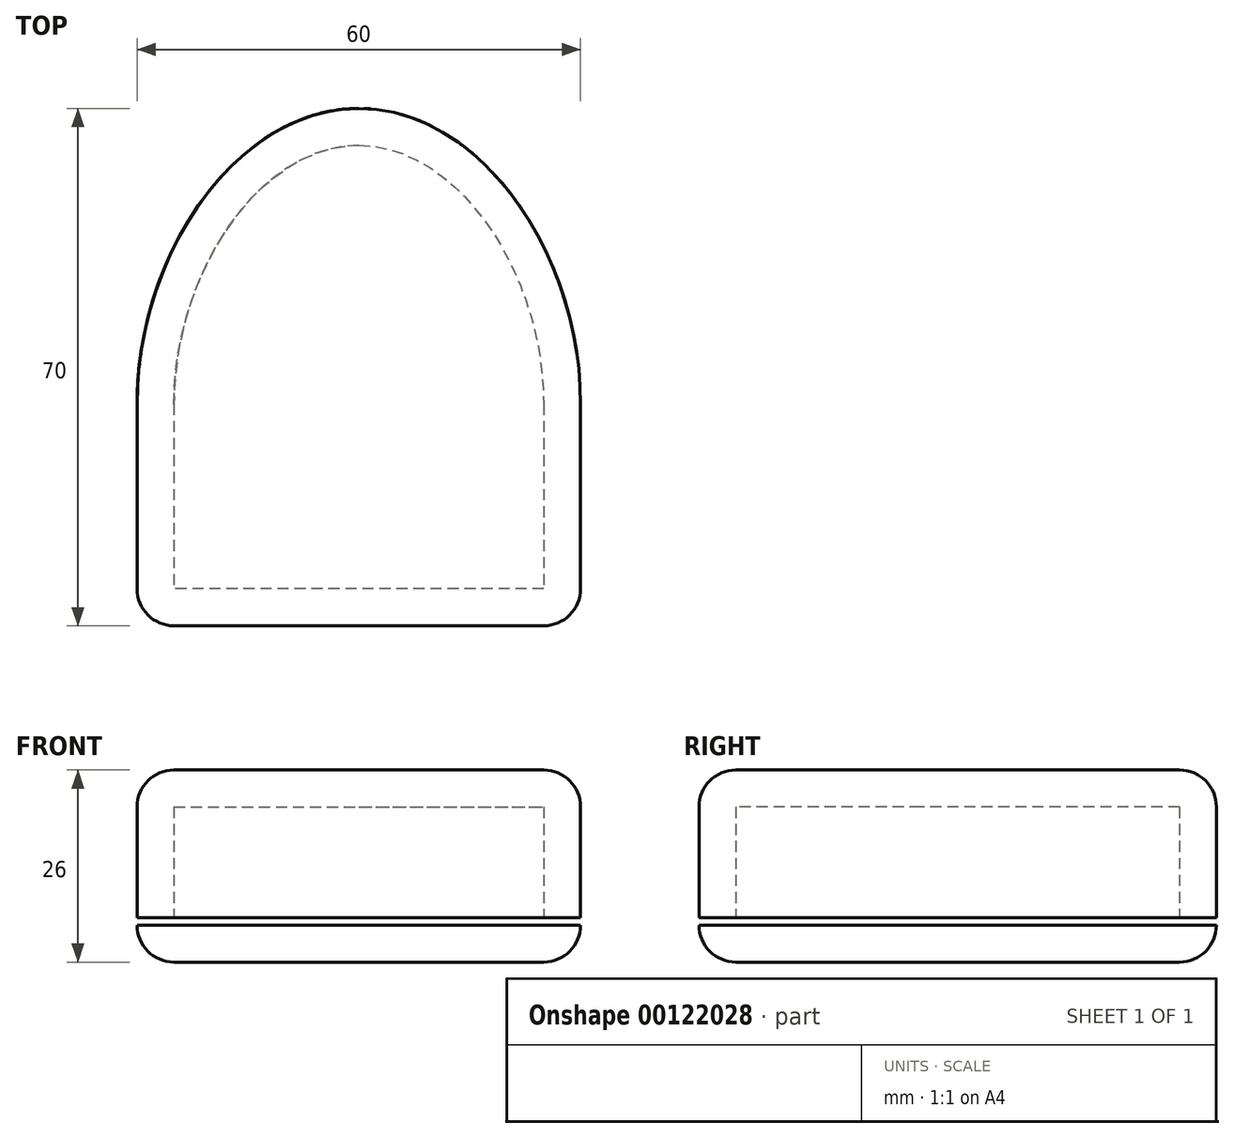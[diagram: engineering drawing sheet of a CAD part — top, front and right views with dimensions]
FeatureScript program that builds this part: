
annotation { "Feature Type Name" : "Feature", "Feature Type Description" : "" }
export const myFeature = defineFeature(function(context is Context, id is Id, definition is map)
    precondition{}
    {
        {
            var Q0;
            Q0=qCreatedBy(makeId("Top.planeOp"),FACE);
            var sketch = newSketch(context, id + "F0", { "sketchPlane" : qUnion([Q0])});
            skLineSegment(sketch, "E0.top", {"start": v(-30, -38.1) * mm, "end": v(30, -38.1) * mm});
            skPoint(sketch, "E0.middle", {"position": v(0, 0) * mm});
            skPoint(sketch, "E1", {"position": v(0, -8.1) * mm});
            skCircle(sketch, "E2", {"center": v(0, -8.1) * mm, "radius": 30 * mm});
            skPoint(sketch, "E3.visualSharp", {"position": v(-30, -38.1) * mm});
            skPoint(sketch, "E4.visualSharp", {"position": v(30, -38.1) * mm});
            skPoint(sketch, "E5", {"position": v(-30, -8.1) * mm});
            skPoint(sketch, "E6", {"position": v(30, -8.1) * mm});
            skFitSpline(sketch, "E7", {"points": [v(0, 31.9) * mm, v(-30, -8.1) * mm], "startDerivative": vector(-49.89, 0) * mm, "endDerivative": vector(0, -60.15) * mm});
            skFitSpline(sketch, "E8.MirrorCS", {"points": [v(0, 31.9) * mm, v(30, -8.1) * mm], "startDerivative": vector(49.89, 0) * mm, "endDerivative": vector(0, -60.15) * mm});
            skLineSegment(sketch, "E9", {"start": v(-30, -8.1) * mm, "end": v(-30, -38.1) * mm});
            skLineSegment(sketch, "E10", {"start": v(30, -8.1) * mm, "end": v(30, -38.1) * mm});
            skSolve(sketch);
        }
        {
            var Q0;
            Q0=qSketchRegion(id+"F0",true);
            extrude(context, id + "F1", {"entities" : qUnion([Q0]), "endBound" : BoundingType.SYMMETRIC, "depth" : 26 * mm});
        }
        {
            var Q0;
            Q0=makeQuery(id+"F1.opExtrude","CAP_EDGE",EDGE,{"disambiguationData":[OSD([sQuery(id+"F0.wireOp",EDGE,"E10")])],"isStart":true});
            var Q1;
            Q1=makeQuery(id+"F1.opExtrude","CAP_EDGE",EDGE,{"disambiguationData":[OSD([sQuery(id+"F0.wireOp",EDGE,"E10")])],"isStart":false});
            var Q2;
            Q2=makeQuery(id+"F1.opExtrude","CAP_EDGE",EDGE,{"disambiguationData":[OSD([sQuery(id+"F0.wireOp",EDGE,"E9")])],"isStart":false});
            var Q3;
            Q3=makeQuery(id+"F1.opExtrude","CAP_EDGE",EDGE,{"disambiguationData":[OSD([sQuery(id+"F0.wireOp",EDGE,"E9")])],"isStart":true});
            fillet(context, id + "F2", {"entities" : qUnion([Q0, Q1, Q2, Q3]), "radius" : 5 * mm, "tangentPropagation" : true, "allowEdgeOverflow" : false});
        }
        {
            var Q0;
            Q0=makeQuery(id+"F1.opExtrude","SWEPT_FACE",FACE,{"disambiguationData":[OSD([sQuery(id+"F0.wireOp",EDGE,"E0.top")])]});
            fillet(context, id + "F3", {"entities" : qUnion([Q0]), "radius" : 5 * mm, "tangentPropagation" : true, "allowEdgeOverflow" : false});
        }
        {
            var Q0;
            Q0=makeQuery(id+"F1.opExtrude","SWEPT_FACE",FACE,{"disambiguationData":[OSD([sQuery(id+"F0.wireOp",EDGE,"E0.top")])]});
            var sketch = newSketch(context, id + "F4", { "sketchPlane" : qUnion([Q0])});
            skLineSegment(sketch, "E11.bottom", {"start": v(0, -8) * mm, "end": v(-33.77, -8) * mm});
            skLineSegment(sketch, "E11.top", {"start": v(0, -7) * mm, "end": v(-33.77, -7) * mm});
            skLineSegment(sketch, "E11.left", {"start": v(0, -8) * mm, "end": v(0, -7) * mm});
            skLineSegment(sketch, "E11.right", {"start": v(-33.77, -8) * mm, "end": v(-33.77, -7) * mm});
            skLineSegment(sketch, "E12.bottom", {"start": v(0, -7) * mm, "end": v(35, -7) * mm});
            skLineSegment(sketch, "E12.top", {"start": v(0, -8) * mm, "end": v(35, -8) * mm});
            skLineSegment(sketch, "E12.left", {"start": v(0, -7) * mm, "end": v(0, -8) * mm});
            skLineSegment(sketch, "E12.right", {"start": v(35, -7) * mm, "end": v(35, -8) * mm});
            skSolve(sketch);
        }
        {
            var Q0;
            Q0 = qSketchRegion(id + "F4", true);
            extrude(context, id + "F5", {"entities" : qUnion([Q0]), "operationType" : NewBodyOperationType.REMOVE, "oppositeDirection" : true, "depth" : 70 * mm});
        }
        {
            var Q0;
            Q0=makeQuery(id+"F5.boolean.opBoolean","COPY",FACE,{"derivedFrom":makeQuery(id+"F5.opExtrude","SWEPT_FACE",FACE,{"disambiguationData":[OSD([sQuery(id+"F4.wireOp",EDGE,"E11.top"),sQuery(id+"F4.wireOp",EDGE,"E12.bottom")])]})});
            shell(context, id + "F6", {"entities" : qUnion([Q0]), "thickness" : 5 * mm});
        }
    });
